# Revit family: 63_UN_LEDPanel_LPS-O 60x60_Norton
name_source: partatom
category: Lighting Fixtures
units: mm (PartAtom-declared; Revit-internal decimal feet)

## family parameters
Always vertical = Yes
Cut with Voids When Loaded = No
Light Source = Yes
OmniClass Number = 23.80.70.11.14.11
OmniClass Title = Downlights
Part Type = Normal
Room Calculation Point = Yes
Round Connector Dimension = Use Diameter
Shared = No
Work Plane-Based = No

## types (7) — shared parameters
Assembly Code = 63.0
Calc_L1_Symbol = 6 mm  [stored 0.019685 ft]
Calc_L2_Symbol = 6 mm  [stored 0.019685 ft]
Color Filter = 16777215
Dimming Lamp Color Temperature Shift = <None>
ETIM Code = -
Emit Shape Visible in Rendering = No
Emit from Rectangle Length = 556 mm  [stored 1.82415 ft]
Emit from Rectangle Width = 556 mm  [stored 1.82415 ft]
GTIN Code = -
H1 = 14 mm  [stored 0.0459318 ft]
Housing_Material = Laminate, White
IK Value = IK06
IP Value = IP20
ISBN Code = -
IfcExportAs = IfcLightFixtureType
IfcExportType = USERDEFINED
L1 = 596 mm  [stored 1.95538 ft]
L2 = 596 mm  [stored 1.95538 ft]
L3 = 20 mm  [stored 0.0656168 ft]
Lamp = LED
Manufacturer = Norton
Model = LPS
Tilt Angle = 90.00°
Type Comments = LPS-O93
URL = https://www.ivlibrary.com
Voltage = 230 V

## per-type parameters (varying)
| type | Apparent Load | Luminous Flux (lm) | Photometric Web File | Wattage Comments |
| LPS-O 865 4100LM 60x60 | 33 VA | 4110 lm | LPS-O 865 4100LM 60x60_LDT.ies | 33 |
| LPS-O 83 3400LM 60x60 | 29 VA | 3400 lm | LPS-O 83 3400LM 60x60_LDT.ies | 29 |
| LPS-O 84 3600LM 60X60 | 29 VA | 3700 lm | LPS-O 84 3600LM 60x60_LDT.ies | 29 |
| LPS-O 83 5300LM 60X60 | 48 VA | 5300 lm | LPS-O 83 5300LM 60x60_LDT.ies | 48 |
| LPS-O 84 4000LM 60x60 | 33 VA | 4000 lm | LPS-O 84 4000LM 60x60_LDT.ies | 33 |
| LPS-O 84 5500LM 60x60 | 48 VA | 5500 lm | LPS-O 84 5500LM 60x60_LDT.ies | 48 |
| LPS-O 865 3700LM 60x60 | 34 VA | 3812 lm | LPS-O 865 3700LM 60x60_LDT.ies | 34 |

note: [stored X ft] marks values corroborated as IEEE doubles in the binary element streams (Revit-internal decimal feet)

## geometry (parser evidence)
native form markers: Sweep x2
no freeform markers — native parametric forms only
